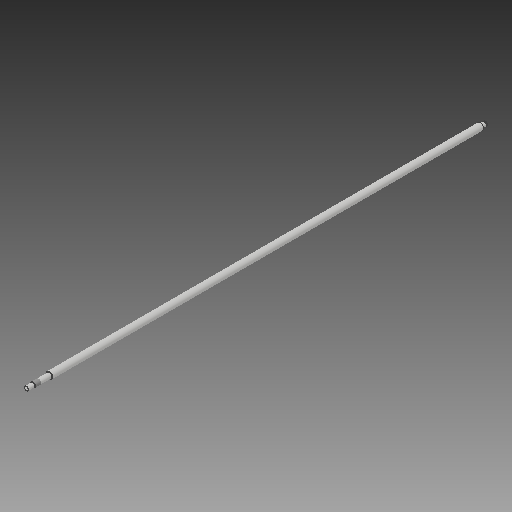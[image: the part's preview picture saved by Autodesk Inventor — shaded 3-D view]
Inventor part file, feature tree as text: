
AUTODESK INVENTOR PART (.ipt)
format: ipt  version: 2018 (Build 220112000, 112)  size: 107,008 bytes
history: native  units: mm
features: extrude x6, sketch x6, other x1, thread x1, chamfer x1
ambient origin geometry x8: Origin, YZ Plane, XZ Plane, XY Plane, X Axis, Y Axis, Z Axis, Center Point
bodies: Body1 (feature_tree)
feature tree (15):
  other  "Sólido1"
  extrude  "Extrusão1"  Depth=1014.5mm TaperAngle=0.0deg
  extrude  "Extrusão2"  Depth=39.0mm TaperAngle=0.0deg
  extrude  "Extrusão3"  Depth=15.0mm TaperAngle=0.0deg
  extrude  "Extrusão4"  Depth=9.15mm TaperAngle=0.0deg
  extrude  "Extrusão5"  Depth=1.15mm TaperAngle=0.0deg
  extrude  "Extrusão6"  Depth=1.85mm TaperAngle=0.0deg
  thread  "Rosca1"  [1 undecoded]
  chamfer  "Chanfro1"  Distance=0.5mm Angle=45.0deg
  sketch  "Esboço1"  dims[d0=16.0mm d1=1014.5mm d2=0.0mm]
  sketch  "Esboço2"  dims[d3=12.0mm d4=39.0mm d5=0.0mm]
  sketch  "Esboço3"  dims[d6=10.0mm d7=15.0mm d8=0.0mm]
  sketch  "Esboço4"  dims[d9=10.0mm d10=9.15mm d11=0.0mm]
  sketch  "Esboço5"  dims[d12=9.0mm d13=1.15mm d14=0.0mm]
  sketch  "Esboço6"  dims[d15=10.0mm d16=1.85mm d17=0.0mm d18=14.0mm d19=0.0mm d20=0.5mm d21=2.0mm d22=45.0deg]
note: 1 required parameter value undecoded (feature->parameter linkage not recoverable at this tier; creation-order binding heuristic only, values carry confidence <= 0.55)
